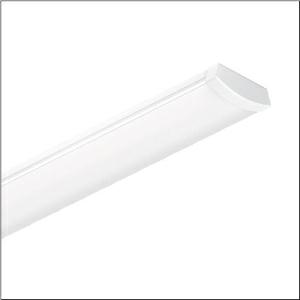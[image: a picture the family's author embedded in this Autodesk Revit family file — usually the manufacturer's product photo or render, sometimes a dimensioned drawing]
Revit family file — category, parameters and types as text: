
# Revit family: siluette_r__21_51ln12mdm20a_d267
name_source: partatom
category: Lighting Fixtures
units: mm (PartAtom-declared; Revit-internal decimal feet)

## family parameters
Cut with Voids When Loaded = No
Host = Face
Light Source = No
Part Type = Normal
Room Calculation Point = No
Round Connector Dimension = Use Diameter
Shared = No

## types (1)
- --- (1 x LED, 1510 lm, 12.2 W, 5000K)
    Apparent Load = 12 VA
    CIE Flux Codes = 43 73 92 94 100
    Color Rendering = 80
    Color Temperature = 5000K
    Default Elevation = 1800 mm
    Description = Siluette® 21, office luminaire, primary optical cover: enclosure, of PC, frosted, light emission: direct distribution, primary light characteristic: symmetric, installation type: suspended mounting, surface-mounted, LED, rated luminous flux: 2.630lm, luminous efficacy: 130lm/W, light colour: 830/840/850, colour temperature: 3000/4000/5000K, with terminal, 3-pole, mains connection: 220..240V, AC, 50/60Hz, rated input power: 20W, housing, of sheet steel, white, length: 600mm, width: 152mm, height: 53mm, end cap, of PMMA, white, protection rating (complete): IP44, insulation class (complete): insulation class I (protective earthing), certification: CE, UKCA, protection symbol: D, permissible operating ambient temperature: -20..+40°C, contact your sales advisor before using the luminaires in applications with unclear chemical exposure, large temperature fluctuations or condensation-forming humidity, corresponds to IFS (International Featured Standards) requirements for safety and quality in the food industry, packaging unit: 1 piece
    Height = 52 mm  [stored 0.170604 ft]
    Lamp = 1 x LED
    Lamp Light Flux = 1510 lm
    Lamp Power = 12.2 W
    Lamp count = 1
    Length = 645 mm
    Luminous efficacy = 124 lm/W
    Manufacturer = Siteco
    ModVariant = No
    Model = 51LN12MDM20A
    Mounting Place = Ceiling
    Mounting Type = Pendant
    Number of Poles = 1
    OnlyDefault = Yes
    Power Factor = 1
    Product Name = Siluette® 21
    Product group = office luminaire | ceiling pendant
    ProductGroupID = 902
    Protection Class = Protection class I
    Protection Degree = IP 44
    RLX_Detail_Level = 1
    RLX_Emergency_Light_Flux = 0 lm
    RLX_Emergency_Type = 0
    RLX_Emergency_Type_DB = No
    RlxData = <blob elided: 20149 chars, md5=1d1c65a4>
    Socket = socket
    Standby Power = 0 W
    System Light Flux = 1510 lm
    System Power = 12 W
    Type Comments = individual setting: colour temperature 5000K, luminous flux: 57 % | (OFF | OFF | ON) | 200 mA
    Type Image = l_1296910.jpg
    URL = http://relux.com
    VarID = @adj_019267
    Voltage = 0 V
    Weight = 0.00 kg
    Width = 152 mm

note: [stored X ft] marks values corroborated as IEEE doubles in the binary element streams (Revit-internal decimal feet)

## geometry (parser evidence)
native form markers: Blend x4, Sweep x12
no freeform markers — native parametric forms only
